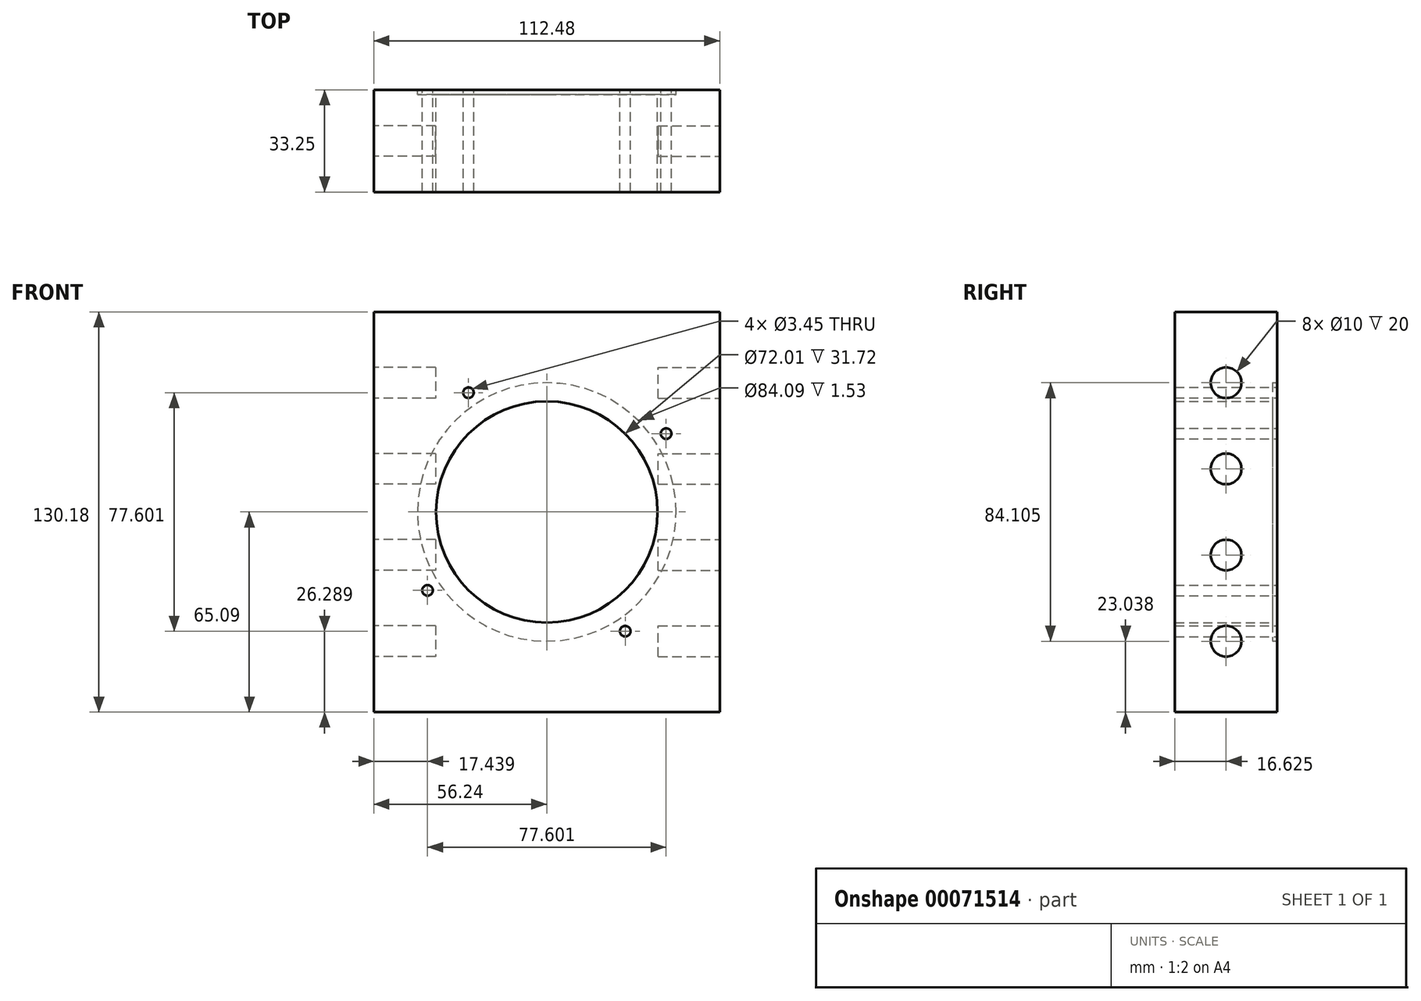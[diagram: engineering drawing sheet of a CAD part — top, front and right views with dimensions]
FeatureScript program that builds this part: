
annotation { "Feature Type Name" : "Feature", "Feature Type Description" : "" }
export const myFeature = defineFeature(function(context is Context, id is Id, definition is map)
    precondition{}
    {
        {
            var Q0;
            Q0=qCreatedBy(makeId("Front.planeOp"),FACE);
            var sketch = newSketch(context, id + "F0", { "sketchPlane" : qUnion([Q0])});
            skLineSegment(sketch, "E0.bottom", {"start": v(-56.24, 65.09) * mm, "end": v(56.24, 65.09) * mm});
            skLineSegment(sketch, "E0.top", {"start": v(-56.24, -65.09) * mm, "end": v(56.24, -65.09) * mm});
            skLineSegment(sketch, "E0.left", {"start": v(-56.24, 65.09) * mm, "end": v(-56.24, -65.09) * mm});
            skLineSegment(sketch, "E0.right", {"start": v(56.24, 65.09) * mm, "end": v(56.24, -65.09) * mm});
            skCircle(sketch, "E1", {"center": v(0, 0) * mm, "radius": 36 * mm});
            skCircle(sketch, "E2", {"center": v(-25.5, 38.8) * mm, "radius": 1.73 * mm});
            skCircle(sketch, "E3.1.0", {"center": v(-38.8, -25.5) * mm, "radius": 1.73 * mm});
            skCircle(sketch, "E3.2.0", {"center": v(25.5, -38.8) * mm, "radius": 1.73 * mm});
            skCircle(sketch, "E3.3.0", {"center": v(38.8, 25.5) * mm, "radius": 1.73 * mm});
            skSolve(sketch);
        }
        {
            var Q0;
            Q0 = qSketchRegion(id + "F0", true);
            extrude(context, id + "F1", {"entities" : qUnion([Q0]), "depth" : 33.25 * mm});
        }
        {
            var Q0;
            Q0=makeQuery(id+"F1.opExtrude","SWEPT_FACE",FACE,{"disambiguationData":[OSD([sQuery(id+"F0.wireOp",EDGE,"E0.left")])]});
            var sketch = newSketch(context, id + "F2", { "sketchPlane" : qUnion([Q0])});
            skCircle(sketch, "E4", {"center": v(16.62, 42.05) * mm, "radius": 5 * mm});
            skCircle(sketch, "E5.0.1.0", {"center": v(16.62, 14.02) * mm, "radius": 5 * mm});
            skCircle(sketch, "E5.0.2.0", {"center": v(16.62, -14.02) * mm, "radius": 5 * mm});
            skCircle(sketch, "E5.0.3.0", {"center": v(16.62, -42.05) * mm, "radius": 5 * mm});
            skLineSegment(sketch, "E5.direction1", {"start": v(16.62, 42.05) * mm, "end": v(42.8, 42.05) * mm, "construction": true});
            skLineSegment(sketch, "E5.direction2", {"start": v(16.62, 42.05) * mm, "end": v(16.62, 14.02) * mm, "construction": true});
            skSolve(sketch);
        }
        {
            var Q0;
            Q0 = qSketchRegion(id + "F2", true);
            extrude(context, id + "F3", {"entities" : qUnion([Q0]), "operationType" : NewBodyOperationType.REMOVE, "oppositeDirection" : true, "depth" : 20 * mm});
        }
        {
            var Q0;
            Q0=makeQuery(id+"F1.opExtrude","SWEPT_FACE",FACE,{"disambiguationData":[OSD([sQuery(id+"F0.wireOp",EDGE,"E0.right")])]});
            var sketch = newSketch(context, id + "F4", { "sketchPlane" : qUnion([Q0])});
            skCircle(sketch, "E6", {"center": v(-16.62, 42.05) * mm, "radius": 5 * mm});
            skCircle(sketch, "E7.0.1.0", {"center": v(-16.62, 14.02) * mm, "radius": 5 * mm});
            skCircle(sketch, "E7.0.2.0", {"center": v(-16.62, -14.02) * mm, "radius": 5 * mm});
            skCircle(sketch, "E7.0.3.0", {"center": v(-16.62, -42.05) * mm, "radius": 5 * mm});
            skLineSegment(sketch, "E7.direction1", {"start": v(-16.62, 42.05) * mm, "end": v(9.56, 42.05) * mm, "construction": true});
            skLineSegment(sketch, "E7.direction2", {"start": v(-16.62, 42.05) * mm, "end": v(-16.62, 14.02) * mm, "construction": true});
            skSolve(sketch);
        }
        {
            var Q0;
            Q0 = qSketchRegion(id + "F4", true);
            extrude(context, id + "F5", {"entities" : qUnion([Q0]), "operationType" : NewBodyOperationType.REMOVE, "oppositeDirection" : true, "depth" : 20 * mm});
        }
        {
            var Q0;
            Q0=makeQuery(id+"F1.opExtrude","CAP_FACE",FACE,{"disambiguationData":[OSD([sQuery(id+"F0.wireOp",EDGE,"E0.bottom"),sQuery(id+"F0.wireOp",EDGE,"E0.top"),sQuery(id+"F0.wireOp",EDGE,"E0.left"),sQuery(id+"F0.wireOp",EDGE,"E0.right"),sQuery(id+"F0.wireOp",EDGE,"E1"),sQuery(id+"F0.wireOp",EDGE,"E2"),sQuery(id+"F0.wireOp",EDGE,"E3.1.0"),sQuery(id+"F0.wireOp",EDGE,"E3.2.0"),sQuery(id+"F0.wireOp",EDGE,"E3.3.0")])],"isStart":true});
            var sketch = newSketch(context, id + "F6", { "sketchPlane" : qUnion([Q0])});
            skCircle(sketch, "E8", {"center": v(0, 0) * mm, "radius": 42.05 * mm});
            skSolve(sketch);
        }
        {
            var Q0;
            Q0 = qSketchRegion(id + "F6", true);
            extrude(context, id + "F7", {"entities" : qUnion([Q0]), "operationType" : NewBodyOperationType.REMOVE, "oppositeDirection" : true, "depth" : 1.53 * mm});
        }
    });
